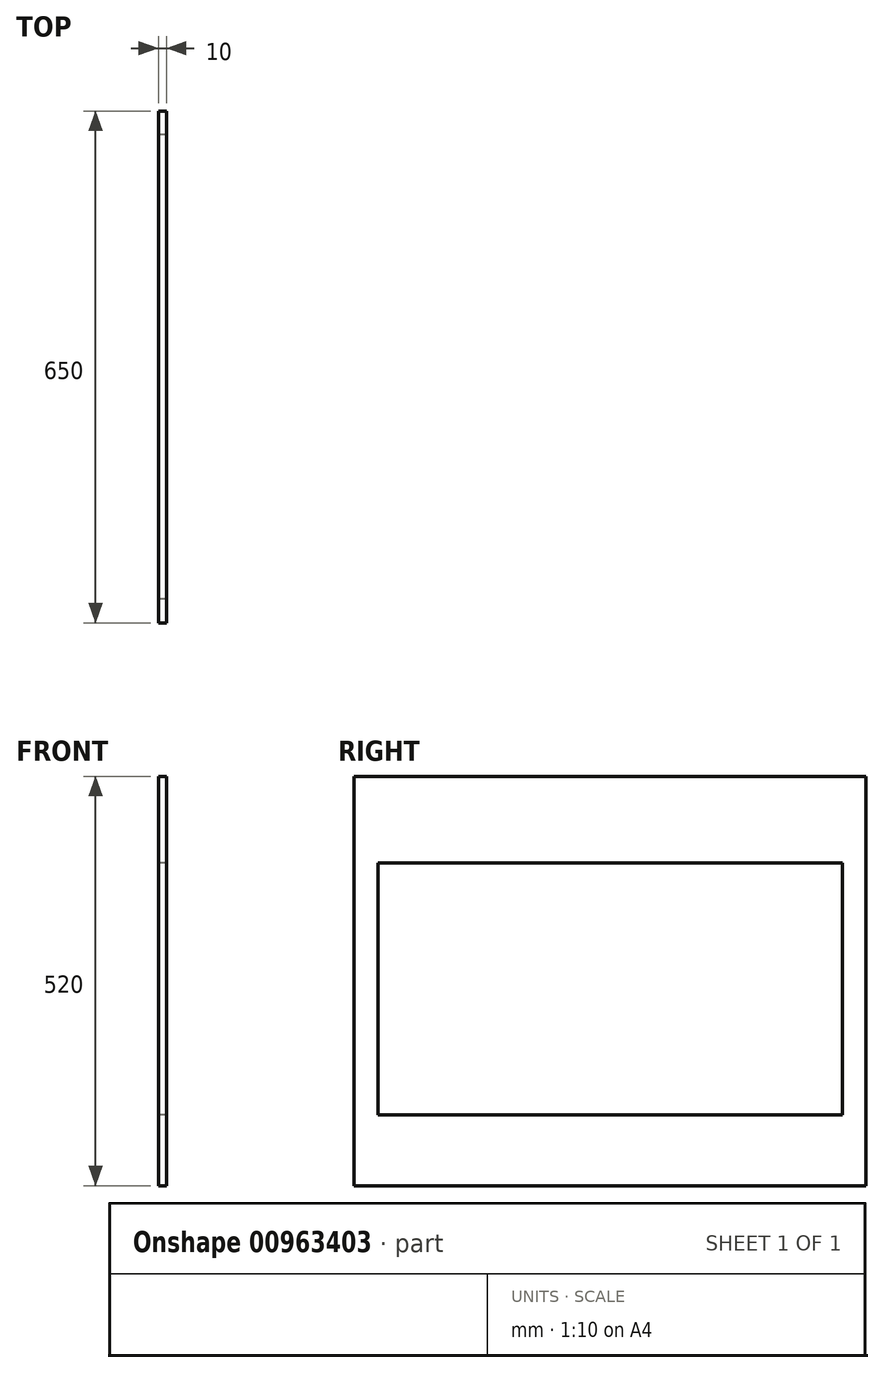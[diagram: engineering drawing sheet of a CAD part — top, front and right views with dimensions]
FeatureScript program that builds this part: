
annotation { "Feature Type Name" : "Feature", "Feature Type Description" : "" }
export const myFeature = defineFeature(function(context is Context, id is Id, definition is map)
    precondition{}
    {
        {
            var Q0;
            Q0=qCreatedBy(makeId("Right.planeOp"),FACE);
            var sketch = newSketch(context, id + "F0", { "sketchPlane" : qUnion([Q0])});
            skLineSegment(sketch, "E0.bottom", {"start": v(-325, -260) * mm, "end": v(325, -260) * mm});
            skLineSegment(sketch, "E0.top", {"start": v(-325, 260) * mm, "end": v(325, 260) * mm});
            skLineSegment(sketch, "E0.left", {"start": v(-325, -260) * mm, "end": v(-325, 260) * mm});
            skLineSegment(sketch, "E0.right", {"start": v(325, -260) * mm, "end": v(325, 260) * mm});
            skPoint(sketch, "E0.middle", {"position": v(0, 0) * mm});
            skLineSegment(sketch, "E1.bottom", {"start": v(-295, 150) * mm, "end": v(295, 150) * mm});
            skLineSegment(sketch, "E1.top", {"start": v(-295, -170) * mm, "end": v(295, -170) * mm});
            skLineSegment(sketch, "E1.left", {"start": v(-295, 150) * mm, "end": v(-295, -170) * mm});
            skLineSegment(sketch, "E1.right", {"start": v(295, 150) * mm, "end": v(295, -170) * mm});
            skSolve(sketch);
        }
        {
            var Q0;
            Q0=makeQuery(id+"F0.imprint","IMPRINT",FACE,{"disambiguationData":[TD([[makeQuery(id+"F0.imprint","IMPRINT",EDGE,{"derivedFrom":sQuery(id+"F0.wireOp",EDGE,"E0.bottom")}),1.0]])]});
            extrude(context, id + "F1", {"entities" : qUnion([Q0]), "depth" : 10 * mm, "offsetDistance" : 25 * mm});
        }
    });
